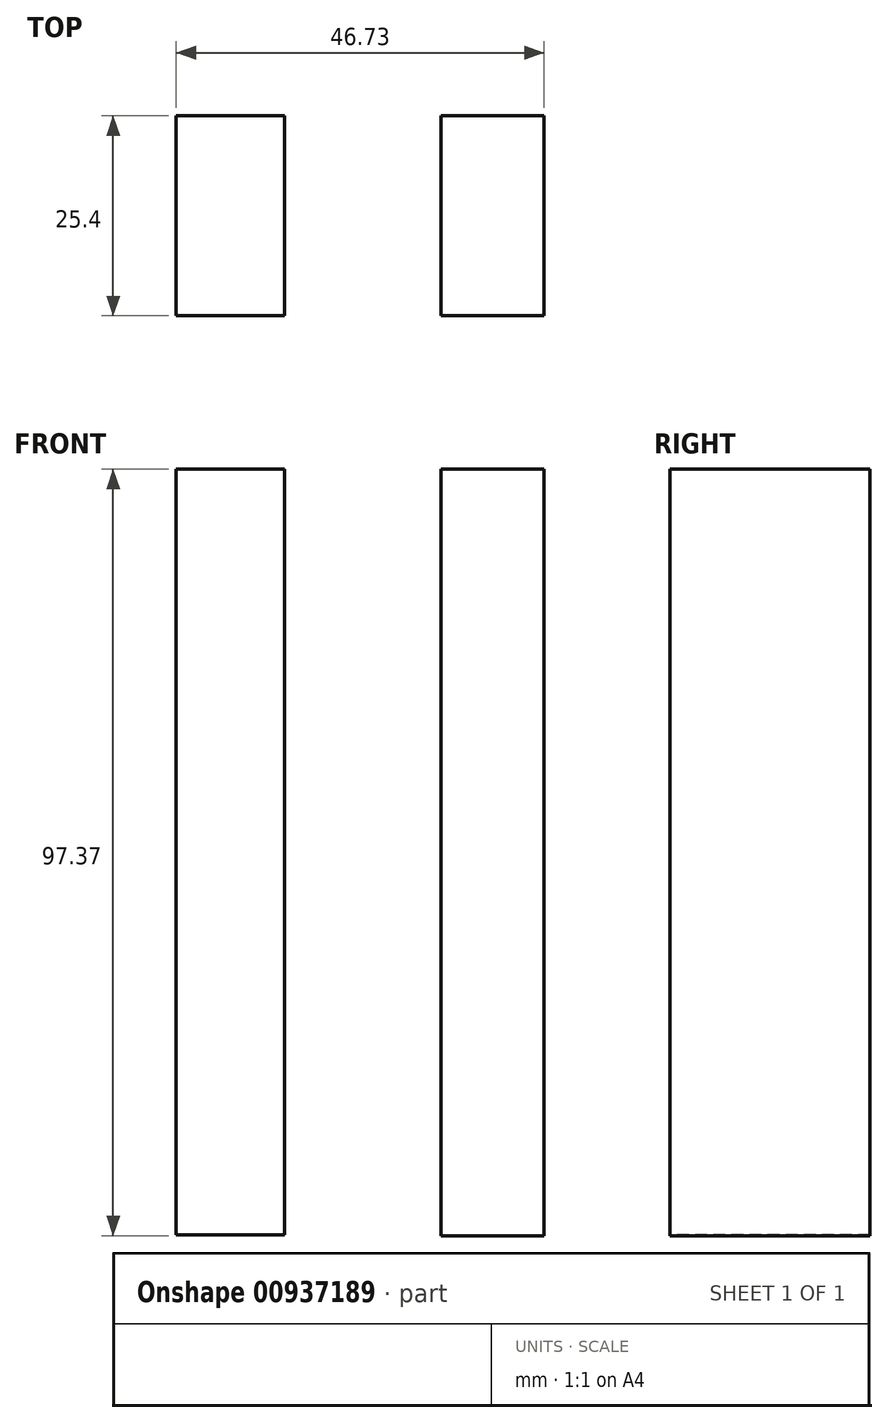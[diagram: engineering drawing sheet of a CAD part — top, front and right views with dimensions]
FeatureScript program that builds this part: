
annotation { "Feature Type Name" : "Feature", "Feature Type Description" : "" }
export const myFeature = defineFeature(function(context is Context, id is Id, definition is map)
    precondition{}
    {
        {
            var Q0;
            Q0=qCreatedBy(makeId("Front.planeOp"),FACE);
            var sketch = newSketch(context, id + "F0", { "sketchPlane" : qUnion([Q0])});
            skLineSegment(sketch, "E0.bottom", {"start": v(-51.36, -47.83) * mm, "end": v(-37.63, -47.83) * mm});
            skLineSegment(sketch, "E0.top", {"start": v(-51.36, 49.43) * mm, "end": v(-37.63, 49.43) * mm});
            skLineSegment(sketch, "E0.left", {"start": v(-51.36, -47.83) * mm, "end": v(-51.36, 49.43) * mm});
            skLineSegment(sketch, "E0.right", {"start": v(-37.63, -47.83) * mm, "end": v(-37.63, 49.43) * mm});
            skLineSegment(sketch, "E1.bottom", {"start": v(-17.74, -47.94) * mm, "end": v(-4.63, -47.94) * mm});
            skLineSegment(sketch, "E1.top", {"start": v(-17.74, 49.43) * mm, "end": v(-4.63, 49.43) * mm});
            skLineSegment(sketch, "E1.left", {"start": v(-17.74, -47.94) * mm, "end": v(-17.74, 49.43) * mm});
            skLineSegment(sketch, "E1.right", {"start": v(-4.63, -47.94) * mm, "end": v(-4.63, 49.43) * mm});
            skSolve(sketch);
        }
        {
            var Q0;
            Q0=sQuery(id+"F0.wireOp",EDGE,"E0.top");
            var Q1;
            Q1=sQuery(id+"F0.wireOp",EDGE,"E1.left");
            var Q2;
            Q2=sQuery(id+"F0.wireOp",EDGE,"E1.right");
            var Q3;
            Q3=sQuery(id+"F0.wireOp",EDGE,"E1.top");
            var Q4;
            Q4=sQuery(id+"F0.wireOp",EDGE,"E0.bottom");
            var Q5;
            Q5=sQuery(id+"F0.wireOp",EDGE,"E1.bottom");
            var Q6;
            Q6=sQuery(id+"F0.wireOp",EDGE,"E0.right");
            var Q7;
            Q7=sQuery(id+"F0.wireOp",EDGE,"E0.left");
            extrude(context, id + "F1", {"bodyType" : ToolBodyType.SURFACE, "surfaceEntities" : qUnion([Q0, Q1, Q2, Q3, Q4, Q5, Q6, Q7]), "depth" : 25.4 * mm, "offsetDistance" : 25.4 * mm});
        }
    });
